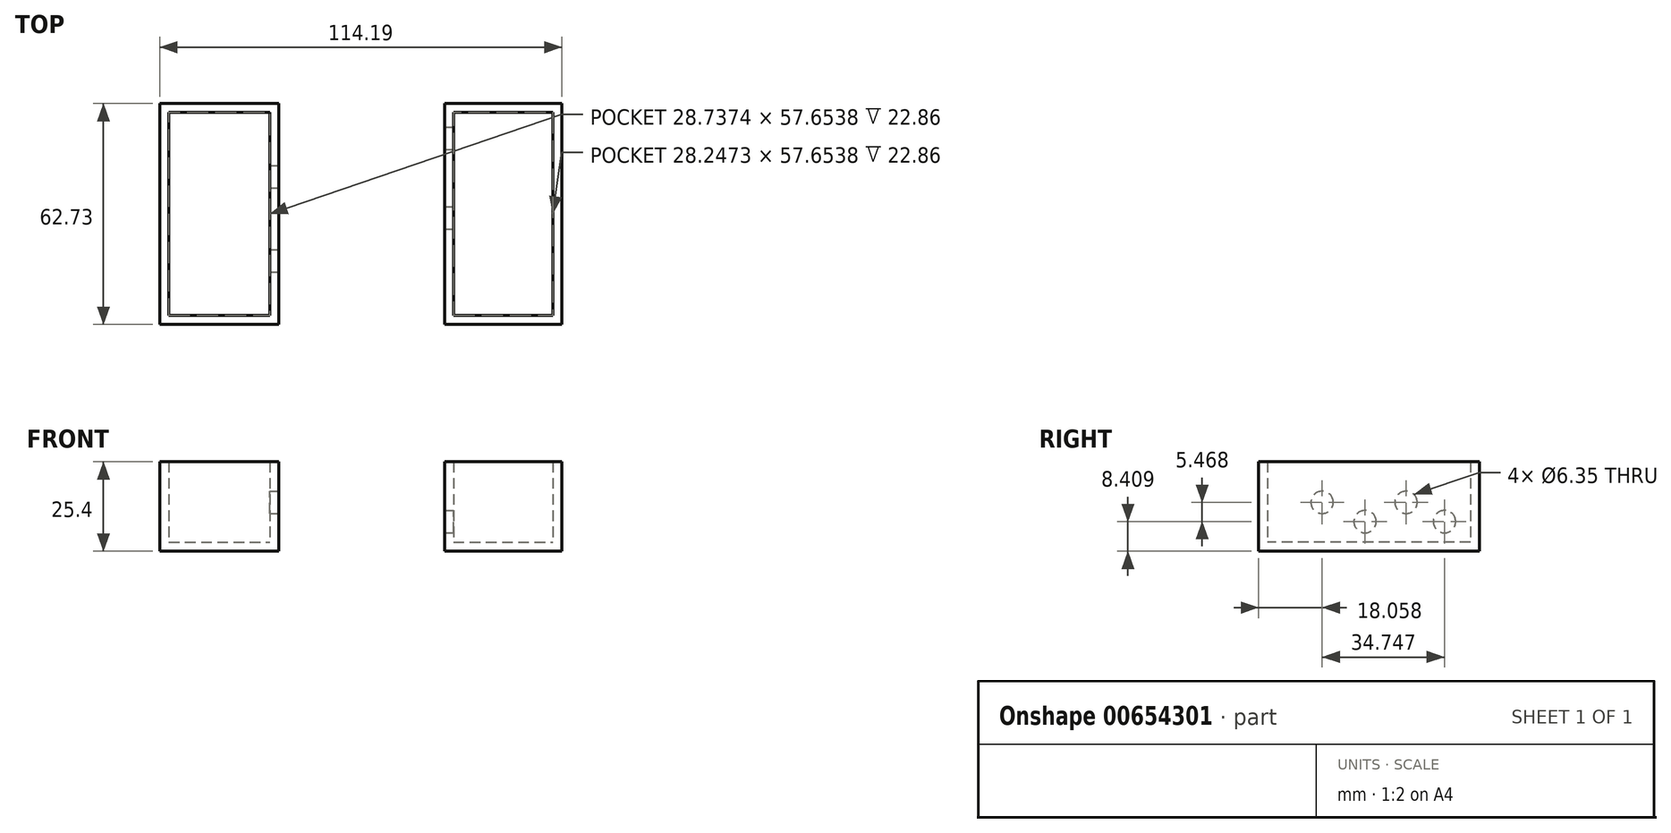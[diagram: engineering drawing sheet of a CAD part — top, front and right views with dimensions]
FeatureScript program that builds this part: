
annotation { "Feature Type Name" : "Feature", "Feature Type Description" : "" }
export const myFeature = defineFeature(function(context is Context, id is Id, definition is map)
    precondition{}
    {
        {
            var Q0;
            Q0=qCreatedBy(makeId("Top.planeOp"),FACE);
            var sketch = newSketch(context, id + "F0", { "sketchPlane" : qUnion([Q0])});
            skLineSegment(sketch, "E0.bottom", {"start": v(-58.2, 20.83) * mm, "end": v(-24.38, 20.83) * mm});
            skLineSegment(sketch, "E0.top", {"start": v(-58.2, -41.9) * mm, "end": v(-24.38, -41.9) * mm});
            skLineSegment(sketch, "E0.left", {"start": v(-58.2, 20.83) * mm, "end": v(-58.2, -41.9) * mm});
            skLineSegment(sketch, "E0.right", {"start": v(-24.38, 20.83) * mm, "end": v(-24.38, -41.9) * mm});
            skLineSegment(sketch, "E1.bottom", {"start": v(22.67, 20.83) * mm, "end": v(56, 20.83) * mm});
            skLineSegment(sketch, "E1.top", {"start": v(22.67, -41.9) * mm, "end": v(56, -41.9) * mm});
            skLineSegment(sketch, "E1.left", {"start": v(22.67, 20.83) * mm, "end": v(22.67, -41.9) * mm});
            skLineSegment(sketch, "E1.right", {"start": v(56, 20.83) * mm, "end": v(56, -41.9) * mm});
            skSolve(sketch);
        }
        {
            var Q0;
            Q0=makeQuery(id+"F0.imprint","IMPRINT",FACE,{"disambiguationData":[TD([[makeQuery(id+"F0.imprint","IMPRINT",EDGE,{"derivedFrom":sQuery(id+"F0.wireOp",EDGE,"E0.bottom")}),-1.0]])]});
            var Q1;
            Q1=makeQuery(id+"F0.imprint","IMPRINT",FACE,{"disambiguationData":[TD([[makeQuery(id+"F0.imprint","IMPRINT",EDGE,{"derivedFrom":sQuery(id+"F0.wireOp",EDGE,"E1.bottom")}),-1.0]])]});
            extrude(context, id + "F1", {"entities" : qUnion([Q0, Q1]), "depth" : 25.4 * mm, "offsetDistance" : 25.4 * mm});
        }
        {
            var Q0;
            Q0=makeQuery(id+"F1.opExtrude","CAP_FACE",FACE,{"disambiguationData":[OSD([sQuery(id+"F0.wireOp",EDGE,"E0.bottom"),sQuery(id+"F0.wireOp",EDGE,"E0.top"),sQuery(id+"F0.wireOp",EDGE,"E0.left"),sQuery(id+"F0.wireOp",EDGE,"E0.right")])],"isStart":false});
            shell(context, id + "F2", {"entities" : qUnion([Q0]), "thickness" : 2.54 * mm});
        }
        {
            var Q0;
            Q0=makeQuery(id+"F1.opExtrude","SWEPT_FACE",FACE,{"disambiguationData":[OSD([sQuery(id+"F0.wireOp",EDGE,"E0.right")])]});
            var sketch = newSketch(context, id + "F3", { "sketchPlane" : qUnion([Q0])});
            skPoint(sketch, "E2", {"position": v(-23.84, 13.88) * mm});
            skPoint(sketch, "E3", {"position": v(0, 13.88) * mm});
            skSolve(sketch);
        }
        {
            var Q0;
            Q0=sQuery(id+"F3.wireOp",VERTEX,"E2");
            var Q1;
            Q1=sQuery(id+"F3.wireOp",VERTEX,"E3");
            var Q2;
            Q2=makeQuery(id+"F1.opExtrude","SWEPT_BODY",BODY,{"disambiguationData":[OSD([sQuery(id+"F0.wireOp",EDGE,"E0.bottom"),sQuery(id+"F0.wireOp",EDGE,"E0.top"),sQuery(id+"F0.wireOp",EDGE,"E0.left"),sQuery(id+"F0.wireOp",EDGE,"E0.right")])]});
            hole(context, id + "F4", {"style" : HoleStyle.SIMPLE, "endStyle" : HoleEndStyle.BLIND, "holeDiameter" : 6.35 * mm, "majorDiameter" : 6.35 * mm, "holeDepth" : 12.7 * mm, "isTappedThrough" : true, "tappedDepth" : 12.7 * mm, "tapClearance" : 3, "locations" : qUnion([Q0, Q1]), "scope" : qUnion([Q2])});
        }
        {
            var Q0;
            Q0=makeQuery(id+"F1.opExtrude","CAP_FACE",FACE,{"disambiguationData":[OSD([sQuery(id+"F0.wireOp",EDGE,"E1.bottom"),sQuery(id+"F0.wireOp",EDGE,"E1.top"),sQuery(id+"F0.wireOp",EDGE,"E1.left"),sQuery(id+"F0.wireOp",EDGE,"E1.right")])],"isStart":false});
            shell(context, id + "F5", {"entities" : qUnion([Q0]), "thickness" : 2.54 * mm});
        }
        {
            var Q0;
            Q0=makeQuery(id+"F5.opShell","OFFSET_FACE",FACE,{"disambiguationData":[OSD([sQuery(id+"F0.wireOp",EDGE,"E1.left")])]});
            var sketch = newSketch(context, id + "F6", { "sketchPlane" : qUnion([Q0])});
            skPoint(sketch, "E4", {"position": v(-11.64, 8.4) * mm});
            skPoint(sketch, "E5", {"position": v(10.9, 8.4) * mm});
            skSolve(sketch);
        }
        {
            var Q0;
            Q0=sQuery(id+"F6.wireOp",VERTEX,"E4");
            var Q1;
            Q1=sQuery(id+"F6.wireOp",VERTEX,"E5");
            var Q2;
            Q2=makeQuery(id+"F1.opExtrude","SWEPT_BODY",BODY,{"disambiguationData":[OSD([sQuery(id+"F0.wireOp",EDGE,"E1.bottom"),sQuery(id+"F0.wireOp",EDGE,"E1.top"),sQuery(id+"F0.wireOp",EDGE,"E1.left"),sQuery(id+"F0.wireOp",EDGE,"E1.right")])]});
            hole(context, id + "F7", {"style" : HoleStyle.SIMPLE, "endStyle" : HoleEndStyle.BLIND, "holeDiameter" : 6.35 * mm, "majorDiameter" : 6.35 * mm, "holeDepth" : 12.7 * mm, "isTappedThrough" : true, "tappedDepth" : 12.7 * mm, "tapClearance" : 3, "locations" : qUnion([Q0, Q1]), "scope" : qUnion([Q2])});
        }
    });
